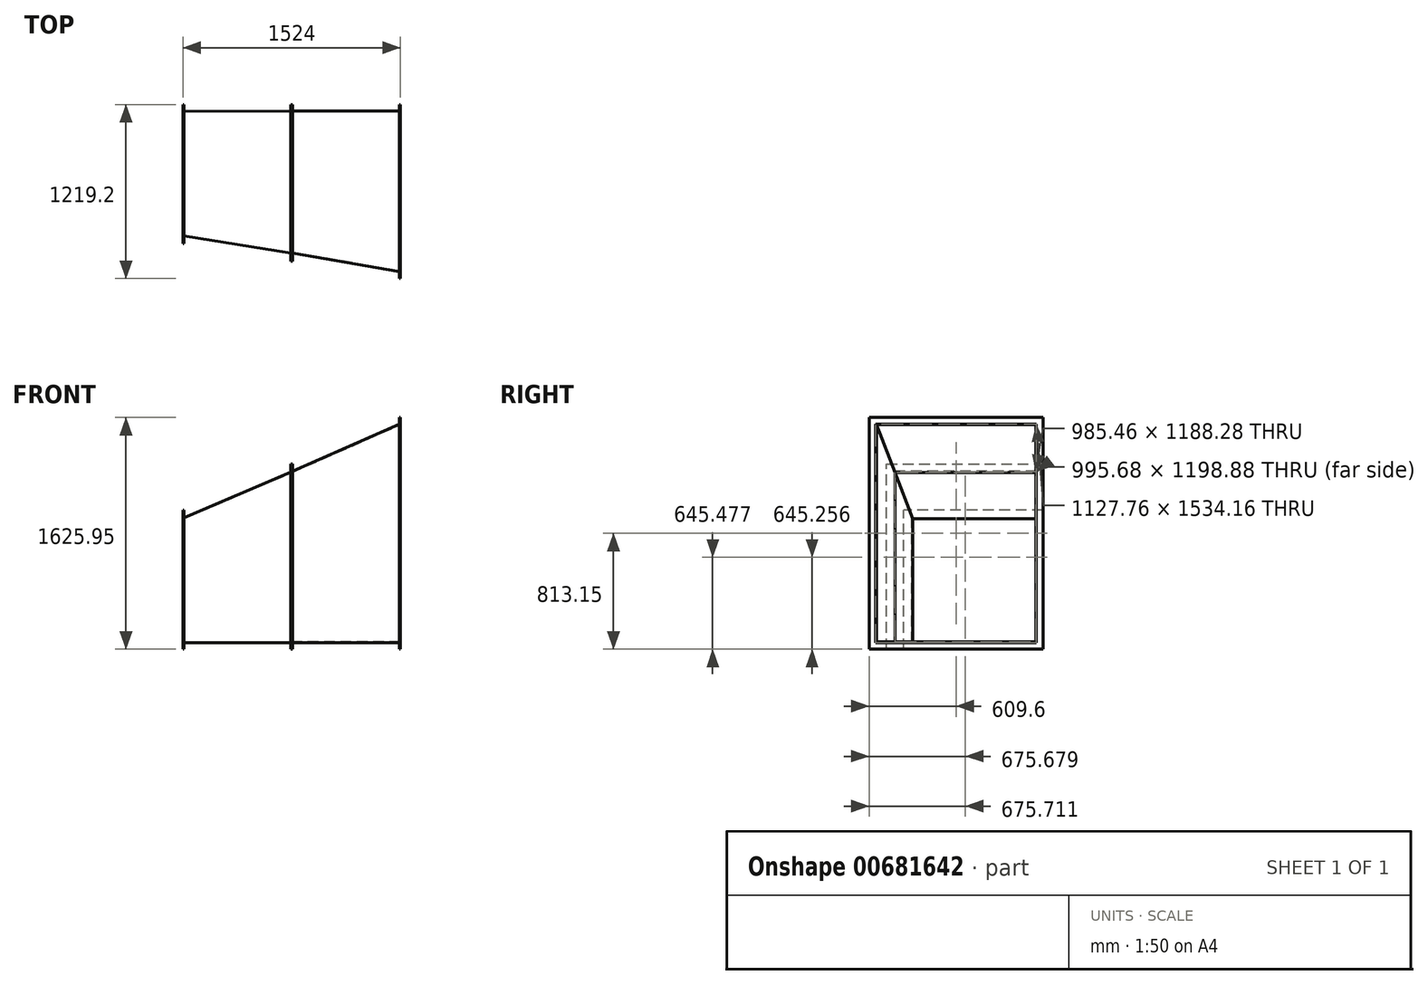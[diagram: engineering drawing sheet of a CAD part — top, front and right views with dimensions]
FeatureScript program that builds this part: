
annotation { "Feature Type Name" : "Feature", "Feature Type Description" : "" }
export const myFeature = defineFeature(function(context is Context, id is Id, definition is map)
    precondition{}
    {
        {
            var Q0;
            Q0=qCreatedBy(makeId("Right.planeOp"),FACE);
            var sketch = newSketch(context, id + "F0", { "sketchPlane" : qUnion([Q0])});
            skLineSegment(sketch, "E0.bottom", {"start": v(563.88, -767.08) * mm, "end": v(-563.88, -767.08) * mm});
            skLineSegment(sketch, "E0.top", {"start": v(563.88, 767.08) * mm, "end": v(-563.88, 767.08) * mm});
            skLineSegment(sketch, "E0.left", {"start": v(563.88, -767.08) * mm, "end": v(563.88, 767.08) * mm});
            skLineSegment(sketch, "E0.right", {"start": v(-563.88, -767.08) * mm, "end": v(-563.88, 767.08) * mm});
            skPoint(sketch, "E0.middle", {"position": v(0, 0) * mm});
            skLineSegment(sketch, "E1.bottom", {"start": v(609.6, -812.8) * mm, "end": v(-609.6, -812.8) * mm});
            skLineSegment(sketch, "E1.top", {"start": v(609.6, 812.8) * mm, "end": v(-609.6, 812.8) * mm});
            skLineSegment(sketch, "E1.left", {"start": v(609.6, -812.8) * mm, "end": v(609.6, 812.8) * mm});
            skLineSegment(sketch, "E1.right", {"start": v(-609.6, -812.8) * mm, "end": v(-609.6, 812.8) * mm});
            skSolve(sketch);
        }
        {
            var Q0;
            Q0=qCreatedBy(makeId("Top.planeOp"),FACE);
            var sketch = newSketch(context, id + "F1", { "sketchPlane" : qUnion([Q0])});
            skLineSegment(sketch, "E2", {"start": v(0, 559.2) * mm, "end": v(-762, 559.2) * mm, "construction": true});
            skLineSegment(sketch, "E3", {"start": v(0, 559.2) * mm, "end": v(0, -558.4) * mm, "construction": true});
            skLineSegment(sketch, "E4", {"start": v(0, -558.4) * mm, "end": v(-762, -431.4) * mm, "construction": true});
            skLineSegment(sketch, "E5", {"start": v(-762, -431.4) * mm, "end": v(-762, 559.2) * mm, "construction": true});
            skLineSegment(sketch, "E6", {"start": v(-762, 559.2) * mm, "end": v(-1524, 559.2) * mm, "construction": true});
            skLineSegment(sketch, "E7", {"start": v(-1524, 559.2) * mm, "end": v(-1524, -304.4) * mm, "construction": true});
            skLineSegment(sketch, "E8", {"start": v(-1524, -304.4) * mm, "end": v(-762, -431.4) * mm, "construction": true});
            skSolve(sketch);
        }
        {
            var Q0;
            Q0=sQuery(id+"F1.wireOp",EDGE,"E5");
            cPlane(context, id + "F2", {"entities" : qUnion([Q0]), "cplaneType" : CPlaneType.LINE_ANGLE, "offset" : 25.4 * mm, "angle" : 90 * degree, "width" : 152.4 * mm, "height" : 152.4 * mm});
        }
        {
            var Q0;
            Q0=qCreatedBy(id+"F2.planeOp",FACE);
            var sketch = newSketch(context, id + "F3", { "sketchPlane" : qUnion([Q0])});
            skLineSegment(sketch, "E9.bottom", {"start": v(-431.76, -767.11) * mm, "end": v(563.92, -767.11) * mm});
            skLineSegment(sketch, "E9.top", {"start": v(-431.76, 431.77) * mm, "end": v(563.92, 431.77) * mm});
            skLineSegment(sketch, "E9.left", {"start": v(-431.76, -767.11) * mm, "end": v(-431.76, 431.77) * mm});
            skLineSegment(sketch, "E9.right", {"start": v(563.92, -767.11) * mm, "end": v(563.92, 431.77) * mm});
            skLineSegment(sketch, "E10.bottom", {"start": v(-487.74, -813.15) * mm, "end": v(609.54, -813.15) * mm});
            skLineSegment(sketch, "E10.top", {"start": v(-487.74, 487.33) * mm, "end": v(609.54, 487.33) * mm});
            skLineSegment(sketch, "E10.left", {"start": v(-487.74, -813.15) * mm, "end": v(-487.74, 487.33) * mm});
            skLineSegment(sketch, "E10.right", {"start": v(609.54, -813.15) * mm, "end": v(609.54, 487.33) * mm});
            skSolve(sketch);
        }
        {
            var Q0;
            Q0=makeQuery(id+"F3.imprint","IMPRINT",FACE,{"disambiguationData":[TD([[makeQuery(id+"F3.imprint","IMPRINT",EDGE,{"derivedFrom":sQuery(id+"F3.wireOp",EDGE,"E9.bottom")}),1.0]])]});
            var Q1;
            Q1=makeQuery(id+"F0.imprint","IMPRINT",FACE,{"disambiguationData":[TD([[makeQuery(id+"F0.imprint","IMPRINT",EDGE,{"derivedFrom":sQuery(id+"F0.wireOp",EDGE,"E0.bottom")}),-1.0]])]});
            loft(context, id + "F4", {"sheetProfilesArray" : [{ "sheetProfileEntities" : qUnion([Q0]) }, { "sheetProfileEntities" : qUnion([Q1]) }]});
        }
        {
            var Q0;
            Q0=makeQuery(id+"F4.opLoft","CAP_FACE",FACE,{"disambiguationData":[OSD([makeQuery(id+"F3.imprint","IMPRINT",FACE,{"disambiguationData":[TD([[makeQuery(id+"F3.imprint","IMPRINT",EDGE,{"derivedFrom":sQuery(id+"F3.wireOp",EDGE,"E9.bottom")}),1.0]])]})])],"isStart":true});
            var Q1;
            Q1=makeQuery(id+"F4.opLoft","CAP_FACE",FACE,{"disambiguationData":[OSD([makeQuery(id+"F0.imprint","IMPRINT",FACE,{"disambiguationData":[TD([[makeQuery(id+"F0.imprint","IMPRINT",EDGE,{"derivedFrom":sQuery(id+"F0.wireOp",EDGE,"E0.bottom")}),-1.0]])]})])],"isStart":true});
            shell(context, id + "F5", {"entities" : qUnion([Q0, Q1]), "thickness" : 5.08 * mm});
        }
        {
            var Q0;
            Q0=makeQuery(id+"F3.imprint","IMPRINT",FACE,{"disambiguationData":[TD([[makeQuery(id+"F3.imprint","IMPRINT",EDGE,{"derivedFrom":sQuery(id+"F3.wireOp",EDGE,"E9.bottom")}),-1.0]])]});
            extrude(context, id + "F6", {"entities" : qUnion([Q0]), "operationType" : NewBodyOperationType.ADD, "depth" : 6.35 * mm, "offsetDistance" : 25.4 * mm});
        }
        {
            var Q0;
            Q0=makeQuery(id+"F0.imprint","IMPRINT",FACE,{"disambiguationData":[TD([[makeQuery(id+"F0.imprint","IMPRINT",EDGE,{"derivedFrom":sQuery(id+"F0.wireOp",EDGE,"E0.bottom")}),1.0]])]});
            extrude(context, id + "F7", {"entities" : qUnion([Q0]), "oppositeDirection" : true, "depth" : 6.35 * mm, "offsetDistance" : 25.4 * mm});
        }
        {
            var Q0;
            Q0=sQuery(id+"F1.wireOp",EDGE,"E7");
            cPlane(context, id + "F8", {"entities" : qUnion([Q0]), "cplaneType" : CPlaneType.LINE_ANGLE, "offset" : 25.4 * mm, "angle" : 90 * degree, "width" : 152.4 * mm, "height" : 152.4 * mm});
        }
        {
            var Q0;
            Q0=makeQuery(id+"F3.imprint","IMPRINT",FACE,{"disambiguationData":[TD([[makeQuery(id+"F3.imprint","IMPRINT",EDGE,{"derivedFrom":sQuery(id+"F3.wireOp",EDGE,"E9.bottom")}),-1.0]])]});
            extrude(context, id + "F9", {"entities" : qUnion([Q0]), "oppositeDirection" : true, "depth" : 6.35 * mm, "offsetDistance" : 25.4 * mm});
        }
        {
            var Q0;
            Q0=qCreatedBy(id+"F8.planeOp",FACE);
            var sketch = newSketch(context, id + "F10", { "sketchPlane" : qUnion([Q0])});
            skLineSegment(sketch, "E11.bottom", {"start": v(563.68, -767.24) * mm, "end": v(-310.08, -767.24) * mm});
            skLineSegment(sketch, "E11.top", {"start": v(563.68, 106.52) * mm, "end": v(-310.08, 106.52) * mm});
            skLineSegment(sketch, "E11.left", {"start": v(563.68, -767.24) * mm, "end": v(563.68, 106.52) * mm});
            skLineSegment(sketch, "E11.right", {"start": v(-310.08, -767.24) * mm, "end": v(-310.08, 106.52) * mm});
            skLineSegment(sketch, "E12.bottom", {"start": v(609.4, -813.14) * mm, "end": v(-365.95, -813.14) * mm});
            skLineSegment(sketch, "E12.top", {"start": v(609.4, 162.22) * mm, "end": v(-365.95, 162.22) * mm});
            skLineSegment(sketch, "E12.left", {"start": v(609.4, -813.14) * mm, "end": v(609.4, 162.22) * mm});
            skLineSegment(sketch, "E12.right", {"start": v(-365.95, -813.14) * mm, "end": v(-365.95, 162.22) * mm});
            skSolve(sketch);
        }
        {
            var Q0;
            Q0=makeQuery(id+"F3.imprint","IMPRINT",FACE,{"disambiguationData":[TD([[makeQuery(id+"F3.imprint","IMPRINT",EDGE,{"derivedFrom":sQuery(id+"F3.wireOp",EDGE,"E9.bottom")}),1.0]])]});
            var Q1;
            Q1=makeQuery(id+"F10.imprint","IMPRINT",FACE,{"disambiguationData":[TD([[makeQuery(id+"F10.imprint","IMPRINT",EDGE,{"derivedFrom":sQuery(id+"F10.wireOp",EDGE,"E11.bottom")}),-1.0]])]});
            loft(context, id + "F11", {"sheetProfilesArray" : [{ "sheetProfileEntities" : qUnion([Q0]) }, { "sheetProfileEntities" : qUnion([Q1]) }]});
        }
        {
            var Q0;
            Q0=makeQuery(id+"F11.opLoft","CAP_FACE",FACE,{"disambiguationData":[OSD([makeQuery(id+"F10.imprint","IMPRINT",FACE,{"disambiguationData":[TD([[makeQuery(id+"F10.imprint","IMPRINT",EDGE,{"derivedFrom":sQuery(id+"F10.wireOp",EDGE,"E11.bottom")}),-1.0]])]})])],"isStart":true});
            var Q1;
            Q1=makeQuery(id+"F11.opLoft","CAP_FACE",FACE,{"disambiguationData":[OSD([makeQuery(id+"F3.imprint","IMPRINT",FACE,{"disambiguationData":[TD([[makeQuery(id+"F3.imprint","IMPRINT",EDGE,{"derivedFrom":sQuery(id+"F3.wireOp",EDGE,"E9.bottom")}),1.0]])]})])],"isStart":true});
            shell(context, id + "F12", {"entities" : qUnion([Q0, Q1]), "thickness" : 5.08 * mm});
        }
        {
            var Q0;
            Q0=makeQuery(id+"F10.imprint","IMPRINT",FACE,{"disambiguationData":[TD([[makeQuery(id+"F10.imprint","IMPRINT",EDGE,{"derivedFrom":sQuery(id+"F10.wireOp",EDGE,"E11.bottom")}),1.0]])]});
            extrude(context, id + "F13", {"entities" : qUnion([Q0]), "operationType" : NewBodyOperationType.ADD, "depth" : 6.35 * mm, "offsetDistance" : 25.4 * mm});
        }
    });
